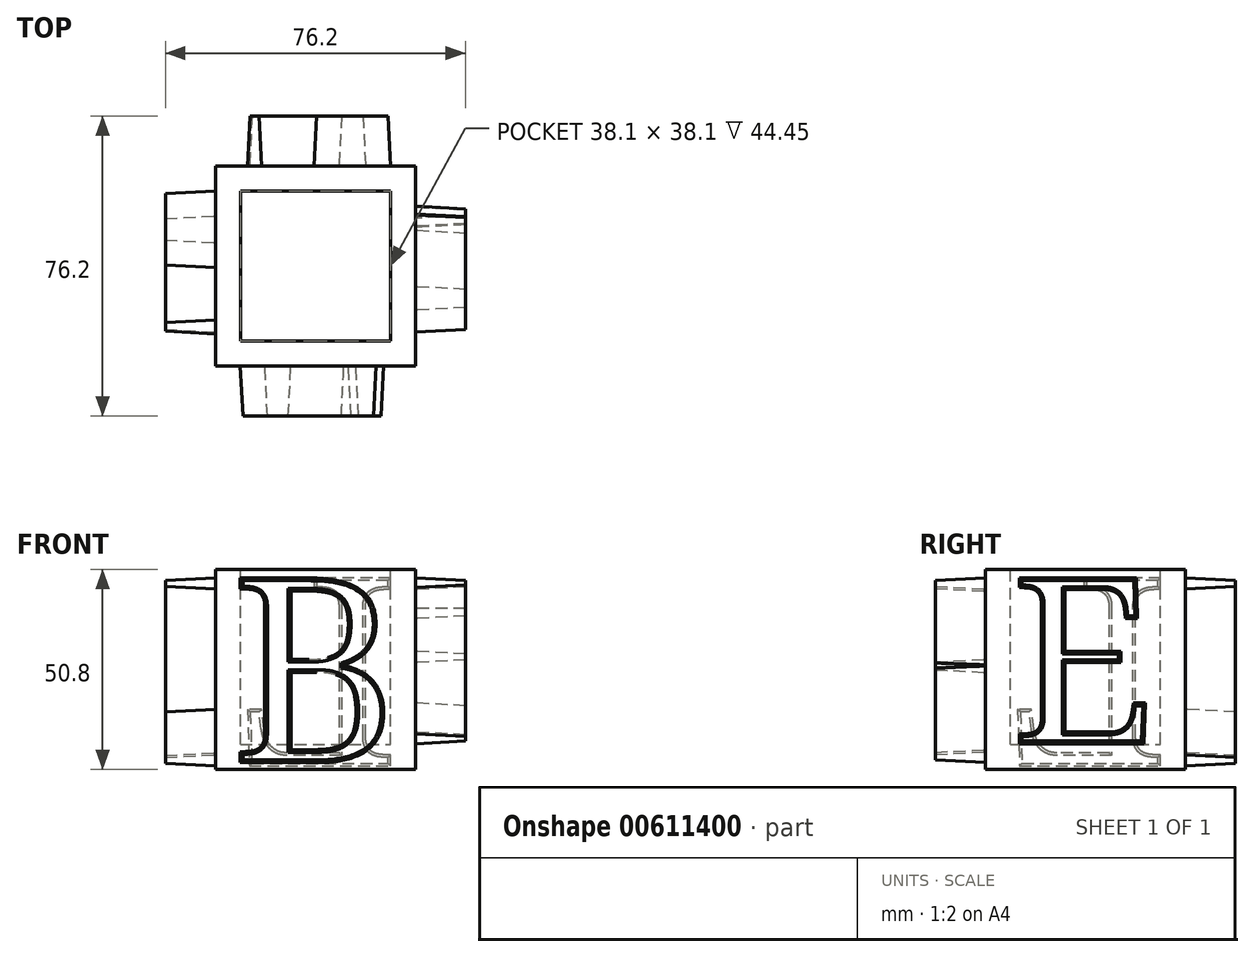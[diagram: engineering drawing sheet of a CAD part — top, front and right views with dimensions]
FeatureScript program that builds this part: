
annotation { "Feature Type Name" : "Feature", "Feature Type Description" : "" }
export const myFeature = defineFeature(function(context is Context, id is Id, definition is map)
    precondition{}
    {
        {
            var Q0;
            Q0=qCreatedBy(makeId("Front.planeOp"),FACE);
            var sketch = newSketch(context, id + "F0", { "sketchPlane" : qUnion([Q0])});
            skLineSegment(sketch, "E0.bottom", {"start": v(0, 0) * mm, "end": v(50.8, 0) * mm});
            skLineSegment(sketch, "E0.top", {"start": v(0, 50.8) * mm, "end": v(50.8, 50.8) * mm});
            skLineSegment(sketch, "E0.left", {"start": v(0, 0) * mm, "end": v(0, 50.8) * mm});
            skLineSegment(sketch, "E0.right", {"start": v(50.8, 0) * mm, "end": v(50.8, 50.8) * mm});
            skSolve(sketch);
        }
        {
            var Q0;
            Q0 = qSketchRegion(id + "F0", true);
            extrude(context, id + "F1", {"entities" : qUnion([Q0]), "depth" : 50.8 * mm, "offsetDistance" : 25.4 * mm});
        }
        {
            var Q0;
            Q0=makeQuery(id+"F1.opExtrude","SWEPT_FACE",FACE,{"disambiguationData":[OSD([sQuery(id+"F0.wireOp",EDGE,"E0.top")])]});
            shell(context, id + "F2", {"entities" : qUnion([Q0]), "thickness" : 6.35 * mm});
        }
        {
            var Q0;
            Q0=makeQuery(id+"F1.opExtrude","CAP_FACE",FACE,{"disambiguationData":[OSD([sQuery(id+"F0.wireOp",EDGE,"E0.bottom"),sQuery(id+"F0.wireOp",EDGE,"E0.top"),sQuery(id+"F0.wireOp",EDGE,"E0.left"),sQuery(id+"F0.wireOp",EDGE,"E0.right")])],"isStart":false});
            var sketch = newSketch(context, id + "F3", { "sketchPlane" : qUnion([Q0])});
            skText(sketch, "E1", { "text": "B", "fontName": "NotoSerif-Regular.ttf"});
            const initialGuessF3  = {"E1": [0.00381, 0.00175, 1, 0, 0.04727]};
            skSetInitialGuess(sketch, initialGuessF3);
            skSolve(sketch);
        }
        {
            var Q0;
            Q0 = qSketchRegion(id + "F3", true);
            extrude(context, id + "F4", {"entities" : qUnion([Q0]), "operationType" : NewBodyOperationType.ADD, "depth" : 12.7 * mm, "offsetDistance" : 25.4 * mm, "hasDraft" : true, "draftAngle" : 3 * degree, "draftPullDirection" : true});
        }
        {
            var Q0;
            Q0=makeQuery(id+"F1.opExtrude","SWEPT_FACE",FACE,{"disambiguationData":[OSD([sQuery(id+"F0.wireOp",EDGE,"E0.right")])]});
            var sketch = newSketch(context, id + "F5", { "sketchPlane" : qUnion([Q0])});
            skText(sketch, "E2", { "text": "E", "fontName": "NotoSerif-Regular.ttf"});
            const initialGuessF5  = {"E2": [-0.04445, 0.00655, 1, 0, 0.04247]};
            skSetInitialGuess(sketch, initialGuessF5);
            skSolve(sketch);
        }
        {
            var Q0;
            Q0 = qSketchRegion(id + "F5", true);
            extrude(context, id + "F6", {"entities" : qUnion([Q0]), "operationType" : NewBodyOperationType.ADD, "depth" : 12.7 * mm, "offsetDistance" : 25.4 * mm, "hasDraft" : true, "draftAngle" : 3 * degree, "draftPullDirection" : true});
        }
        {
            var Q0;
            Q0=makeQuery(id+"F1.opExtrude","CAP_FACE",FACE,{"disambiguationData":[OSD([sQuery(id+"F0.wireOp",EDGE,"E0.bottom"),sQuery(id+"F0.wireOp",EDGE,"E0.top"),sQuery(id+"F0.wireOp",EDGE,"E0.left"),sQuery(id+"F0.wireOp",EDGE,"E0.right")])],"isStart":true});
            var sketch = newSketch(context, id + "F7", { "sketchPlane" : qUnion([Q0])});
            skText(sketch, "E3", { "text": "L", "fontName": "NotoSerif-Regular.ttf"});
            const initialGuessF7  = {"E3": [-0.047, 0.0009, 1, 0, 0.04813]};
            skSetInitialGuess(sketch, initialGuessF7);
            skSolve(sketch);
        }
        {
            var Q0;
            Q0 = qSketchRegion(id + "F7", true);
            extrude(context, id + "F8", {"entities" : qUnion([Q0]), "operationType" : NewBodyOperationType.ADD, "depth" : 12.7 * mm, "offsetDistance" : 25.4 * mm, "hasDraft" : true, "draftAngle" : 3 * degree, "draftPullDirection" : true});
        }
        {
            var Q0;
            Q0=makeQuery(id+"F1.opExtrude","SWEPT_FACE",FACE,{"disambiguationData":[OSD([sQuery(id+"F0.wireOp",EDGE,"E0.left")])]});
            var sketch = newSketch(context, id + "F9", { "sketchPlane" : qUnion([Q0])});
            skText(sketch, "E4", { "text": "L", "fontName": "NotoSerif-Regular.ttf"});
            const initialGuessF9  = {"E4": [0.0038, 0.0009, 1, 0, 0.04813]};
            skSetInitialGuess(sketch, initialGuessF9);
            skSolve(sketch);
        }
        {
            var Q0;
            Q0 = qSketchRegion(id + "F9", true);
            extrude(context, id + "F10", {"entities" : qUnion([Q0]), "operationType" : NewBodyOperationType.ADD, "depth" : 12.7 * mm, "offsetDistance" : 25.4 * mm, "hasDraft" : true, "draftAngle" : 3 * degree, "draftPullDirection" : true});
        }
    });
